# Revit family: ConnectionPipe-BathSpoutConnectionPipe-WallMounted-Vitra-OtherSeries-A45652
name_source: partatom
category: Plumbing Fixtures
revit_build: Autodesk Revit 2017 (Build: 20160225_1515(x64)
units: mm (PartAtom-declared; Revit-internal decimal feet)

## family parameters
Always vertical = No
Cut with Voids When Loaded = No
OmniClass Number = 23.45.55.17
OmniClass Title = Mixing Faucets
Part Type = Normal
Room Calculation Point = No
Round Connector Dimension = Use Diameter
Shared = Yes
Work Plane-Based = Yes

## types (5) — shared parameters
BIMobject category = Bath/Shower Mixer
Brand = VitrA
CW Connection = Yes
Connection Diameter (mm) = 15 mm  [stored 0.0492126 ft]
Default Elevation = 850 mm  [stored 2.78871 ft]
Description = Long Connection Pipe - Wall Mounted
Design country = Turkey
HW Connection = Yes
Hot Water Supply (max.) = 80 °C
Hot Water temperature, factory set to = 38 °C
IFC Classification = Sanitary Terminal
Manufacturer = Vitra
Manufacturer name = Vitra
Masterformat 2014 Code = 22 40 00
Masterformat 2014 Description = Plumbing Fixtures
Min. flow pressure of = 0.5 bar
Mounting type = Pipe Connect
NBS Referans Code = 45-35-70/371
NBS Referans Description = Water supply fittings for wash basins and troughs
Nominal Depth (mm) = 360 mm
Nominal Height (mm) = 95 mm
Nominal Width (mm) = 50 mm  [stored 0.164042 ft]
Number Of Connections = 1
OmniClass Code = 23.45.55.17
OmniClass Description = Mixing Faucets
Product Type = Connection Pipe
Product certification = https://www.vitraglobal.com
Product group = Connection Pipe
Range of Hot Water Supply = 5 - 65 °C
Range of flow pressure = 1 - 5 bar
Test Pressure = 16 bar
UNSPSC Code = 301815
URL = https://vitraglobal.com
Uniclass 1.4 Code = L725111
Uniclass 1.4 Description = Mixer taps
Uniclass 2.0 Code = Pr_40_20_87_09
Uniclass 2.0 Description = Mixer taps
Uniclass 2015 Code = Pr_40_20_87_98
Uniclass 2015 Name = Bath taps
Uniformat II Code = 22 40 00
Uniformat II Description = Plumbing Fixture
Vent Connection = No
Warranty Period (Year) = 5 Years
Waste Connection = No
Weight Net (kg) = 0.5
Youtube = https://www.youtube.com

## per-type parameters (varying)
| type | Article No. (default) | Coating Material | Model | Product SKU | Product url | Technical description |
| ConnectionPipe-BathSpoutConnectionPipe-WallMounted-Vitra-OtherSeries-A45652 | A45652 | Chrome (Metal) | A45652 | A45652 | https://www.vitra.com.tr | https://www.vitra.com.tr |
| ConnectionPipe-BathSpoutConnectionPipe-WallMounted-Vitra-OtherSeries-A4565226 | A4565226 | Copper (Metal) | A4565226 | A4565226 | https://www.vitra.com.tr | https://www.vitra.com.tr |
| ConnectionPipe-BathSpoutConnectionPipe-WallMounted-Vitra-OtherSeries-A4565234 | A4565234 | Brushed Nickel (Metal) | A4565234 | A4565234 | https://www.vitra.com.tr | https://www.vitra.com.tr |
| ConnectionPipe-BathSpoutConnectionPipe-WallMounted-Vitra-OtherSeries-A4565236 | A4565236 | Matte Black (Metal) | A4565236 | A4565236 | https://www.vitra.com.tr | https://www.vitra.com.tr |
| ConnectionPipe-BathSpoutConnectionPipe-WallMounted-Vitra-OtherSeries-A45652EXP | A45652EXP | Chrome (Metal) | A45652EXP | A45652EXP | https://www.vitraglobal.com | https://www.vitraglobal.com |

note: [stored X ft] marks values corroborated as IEEE doubles in the binary element streams (Revit-internal decimal feet)

## geometry (parser evidence)
native form markers: Sweep x2
no freeform markers — native parametric forms only
